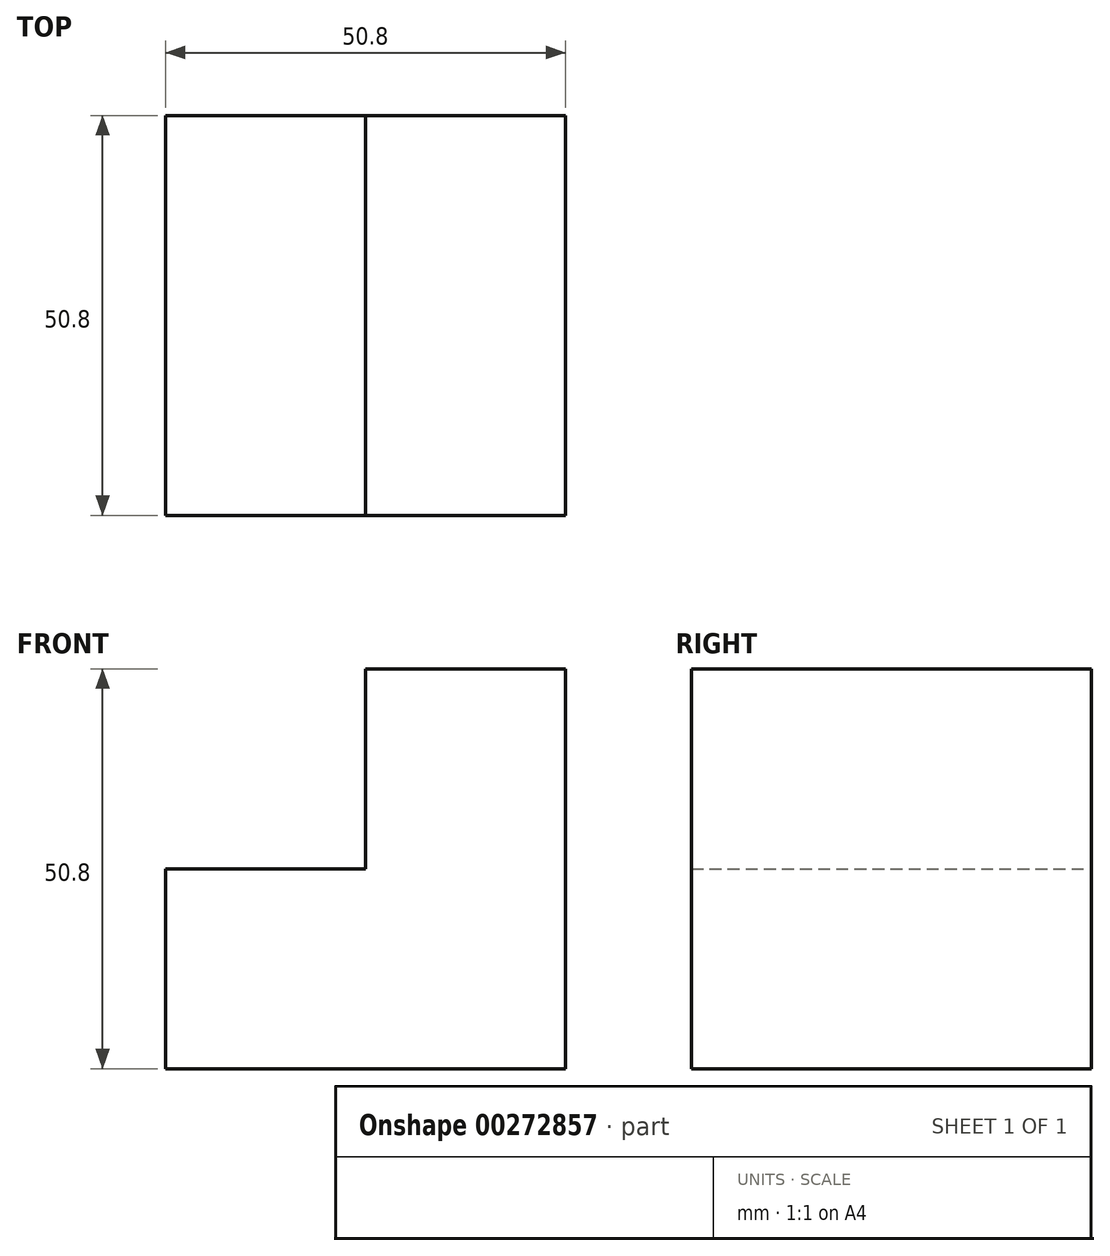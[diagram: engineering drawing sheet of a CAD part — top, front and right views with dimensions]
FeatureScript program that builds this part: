
annotation { "Feature Type Name" : "Feature", "Feature Type Description" : "" }
export const myFeature = defineFeature(function(context is Context, id is Id, definition is map)
    precondition{}
    {
        {
            var Q0;
            Q0=qCreatedBy(makeId("Front.planeOp"),FACE);
            var sketch = newSketch(context, id + "F0", { "sketchPlane" : qUnion([Q0])});
            skLineSegment(sketch, "E0", {"start": v(0, 0) * mm, "end": v(50.8, 0) * mm});
            skLineSegment(sketch, "E1", {"start": v(50.8, 0) * mm, "end": v(50.8, 50.8) * mm});
            skLineSegment(sketch, "E2", {"start": v(50.8, 50.8) * mm, "end": v(25.4, 50.8) * mm});
            skLineSegment(sketch, "E3", {"start": v(25.4, 50.8) * mm, "end": v(25.4, 25.4) * mm});
            skLineSegment(sketch, "E4", {"start": v(25.4, 25.4) * mm, "end": v(0, 25.4) * mm});
            skLineSegment(sketch, "E5", {"start": v(0, 25.4) * mm, "end": v(0, 0) * mm});
            skSolve(sketch);
        }
        {
            var Q0;
            Q0 = qSketchRegion(id + "F0", true);
            extrude(context, id + "F1", {"entities" : qUnion([Q0]), "depth" : 50.8 * mm});
        }
    });
